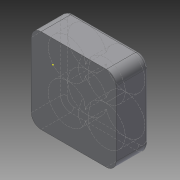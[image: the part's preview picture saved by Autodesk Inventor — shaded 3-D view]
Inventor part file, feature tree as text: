
AUTODESK INVENTOR PART (.ipt)
format: ipt  version: 2015 (Build 190159000, 159)  size: 180,736 bytes
history: native  units: mm
features: fillet x6, hole x4, sketch x3, extrude x1
ambient origin geometry x8: Origin, YZ Plane, XZ Plane, XY Plane, X Axis, Y Axis, Z Axis, Center Point
bodies: Solid1 (feature_tree)
feature tree (14):
  sketch  "Sketch1"  dims[d0=26.0mm d1=26.0mm d2=10.0mm d3=0.0mm d4=3.0mm d5=3.0mm]
  extrude  "Extrusion1"  Depth=3.0mm
  fillet  "Fillet1"  Radius=10.0mm
  fillet  "Fillet2"  Radius=3.0mm
  fillet  "Fillet3"  Radius=3.0mm
  hole  "Hole1"  [1 undecoded]
  hole  "Hole2"  [1 undecoded]
  hole  "Hole3"  [1 undecoded]
  hole  "Hole4"  [1 undecoded]
  fillet  "Fillet4"  [1 undecoded]
  fillet  "Fillet5"  [1 undecoded]
  sketch  "Sketch3"  dims[d7=7.2mm d8=7.0mm d9=12.0mm d10=6.0mm d11=4.0mm d12=2.0mm d13=90.0deg d14=6.0mm d15=20.594885mm d16=7.2mm d17=7.0mm d18=12.0mm d19=6.0mm d20=4.0mm d21=2.0mm d22=90.0deg d23=6.0mm d24=20.594885mm d25=7.0mm d26=7.2mm d27=12.0mm d28=6.0mm d29=4.0mm d30=2.0mm d31=90.0deg d32=6.0mm d33=20.594885mm d34=7.2mm d35=7.0mm d36=12.0mm d37=6.0mm d38=4.0mm d39=2.0mm d40=90.0deg d41=6.0mm d42=20.594885mm d45=3.0mm d46=3.0mm d47=1.0mm]
  fillet  "Fillet6"  [1 undecoded]
  sketch  "Sketch2"  dims[d6=3.0mm]
note: 7 required parameter values undecoded (feature->parameter linkage not recoverable at this tier; creation-order binding heuristic only, values carry confidence <= 0.55)
